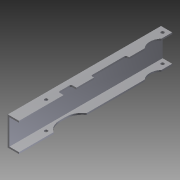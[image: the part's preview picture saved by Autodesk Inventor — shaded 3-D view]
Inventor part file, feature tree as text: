
AUTODESK INVENTOR PART (.ipt)
format: ipt  version: 2012 (Build 160160000, 160)  size: 143,360 bytes
history: native  units: in
note: dims shown in document units (in); Inventor stores cm internally (conversion verified against a paired STEP export)
features: extrude x3, sketch x3, fillet x1
ambient origin geometry x8: Origin, YZ Plane, XZ Plane, XY Plane, X Axis, Y Axis, Z Axis, Center Point
bodies: Solid1 (feature_tree)
feature tree (7):
  extrude  "Extrusion1"  Depth=0.125in
  extrude  "Extrusion2"  Depth=2.25in
  extrude  "Extrusion3"  Depth=12.0in TaperAngle=0.0deg
  fillet  "Fillet1"  Radius=0.125in
  sketch  "Sketch1"  dims[d0=0.125in d1=0.125in]
  sketch  "Sketch2"  dims[d2=0.125in d3=2.25in]
  sketch  "Sketch3"  dims[d4=0.875in d5=12.0in d6=0.0in d9=0.125in d10=0.0in d11=3.375in d12=2.75in d13=0.25in d14=7.5in d15=1.0in d16=0.45in d17=1.25in d18=0.5in d19=7.75in d20=0.3125in d21=0.125in d22=0.0in d23=0.125in d24=1.0in d25=1.625in d26=1.5in d27=0.5in d28=0.375in d29=0.25in d30=9.5in]
